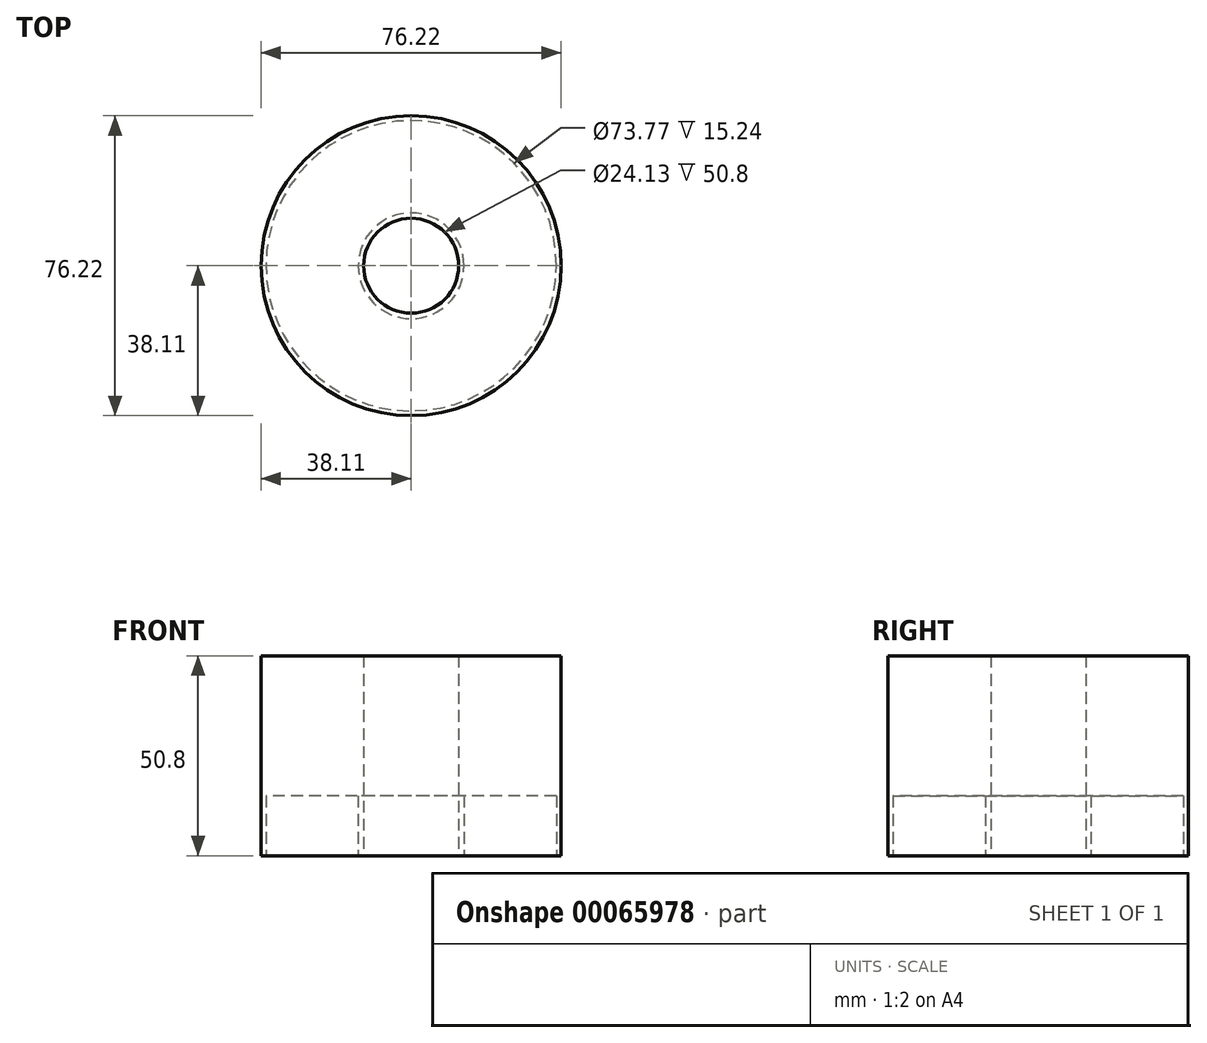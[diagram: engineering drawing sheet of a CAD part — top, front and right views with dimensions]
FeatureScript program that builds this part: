
annotation { "Feature Type Name" : "Feature", "Feature Type Description" : "" }
export const myFeature = defineFeature(function(context is Context, id is Id, definition is map)
    precondition{}
    {
        {
            var Q0;
            Q0=qCreatedBy(makeId("Top.planeOp"),FACE);
            var sketch = newSketch(context, id + "F0", { "sketchPlane" : qUnion([Q0])});
            skCircle(sketch, "E0", {"center": v(0, 0) * mm, "radius": 38.11 * mm});
            skSolve(sketch);
        }
        {
            var Q0;
            Q0 = qSketchRegion(id + "F0", true);
            extrude(context, id + "F1", {"entities" : qUnion([Q0]), "depth" : 50.8 * mm});
        }
        {
            var Q0;
            Q0=qCreatedBy(makeId("Top.planeOp"),FACE);
            var sketch = newSketch(context, id + "F2", { "sketchPlane" : qUnion([Q0])});
            skCircle(sketch, "E1", {"center": v(0, 0) * mm, "radius": 11.49 * mm});
            skCircle(sketch, "E2", {"center": v(0, 0) * mm, "radius": 13.44 * mm});
            skCircle(sketch, "E3", {"center": v(0, 0) * mm, "radius": 36.89 * mm});
            skSolve(sketch);
        }
        {
            var Q0;
            Q0=makeQuery(id+"F2.imprint","IMPRINT",FACE,{"disambiguationData":[TD([[makeQuery(id+"F2.imprint","IMPRINT",EDGE,{"derivedFrom":sQuery(id+"F2.wireOp",EDGE,"E2")}),-1.0]])]});
            extrude(context, id + "F3", {"entities" : qUnion([Q0]), "operationType" : NewBodyOperationType.REMOVE, "depth" : 15.24 * mm});
        }
        {
            var Q0;
            Q0=qCreatedBy(makeId("Top.planeOp"),FACE);
            var sketch = newSketch(context, id + "F4", { "sketchPlane" : qUnion([Q0])});
            skCircle(sketch, "E4", {"center": v(0, 0) * mm, "radius": 11.96 * mm});
            skSolve(sketch);
        }
        {
            var Q0;
            Q0=sQuery(id+"F4.wireOp",VERTEX,"E4.center");
            var Q1;
            Q1=makeQuery(id+"F1.opExtrude","SWEPT_BODY",BODY,{"disambiguationData":[OSD([sQuery(id+"F0.wireOp",EDGE,"E0")])]});
            hole(context, id + "F5", {"style" : HoleStyle.SIMPLE, "endStyle" : HoleEndStyle.THROUGH, "oppositeDirection" : true, "holeDiameter" : 24.13 * mm, "locations" : qUnion([Q0]), "scope" : qUnion([Q1]), "isTappedThrough" : true});
        }
    });
